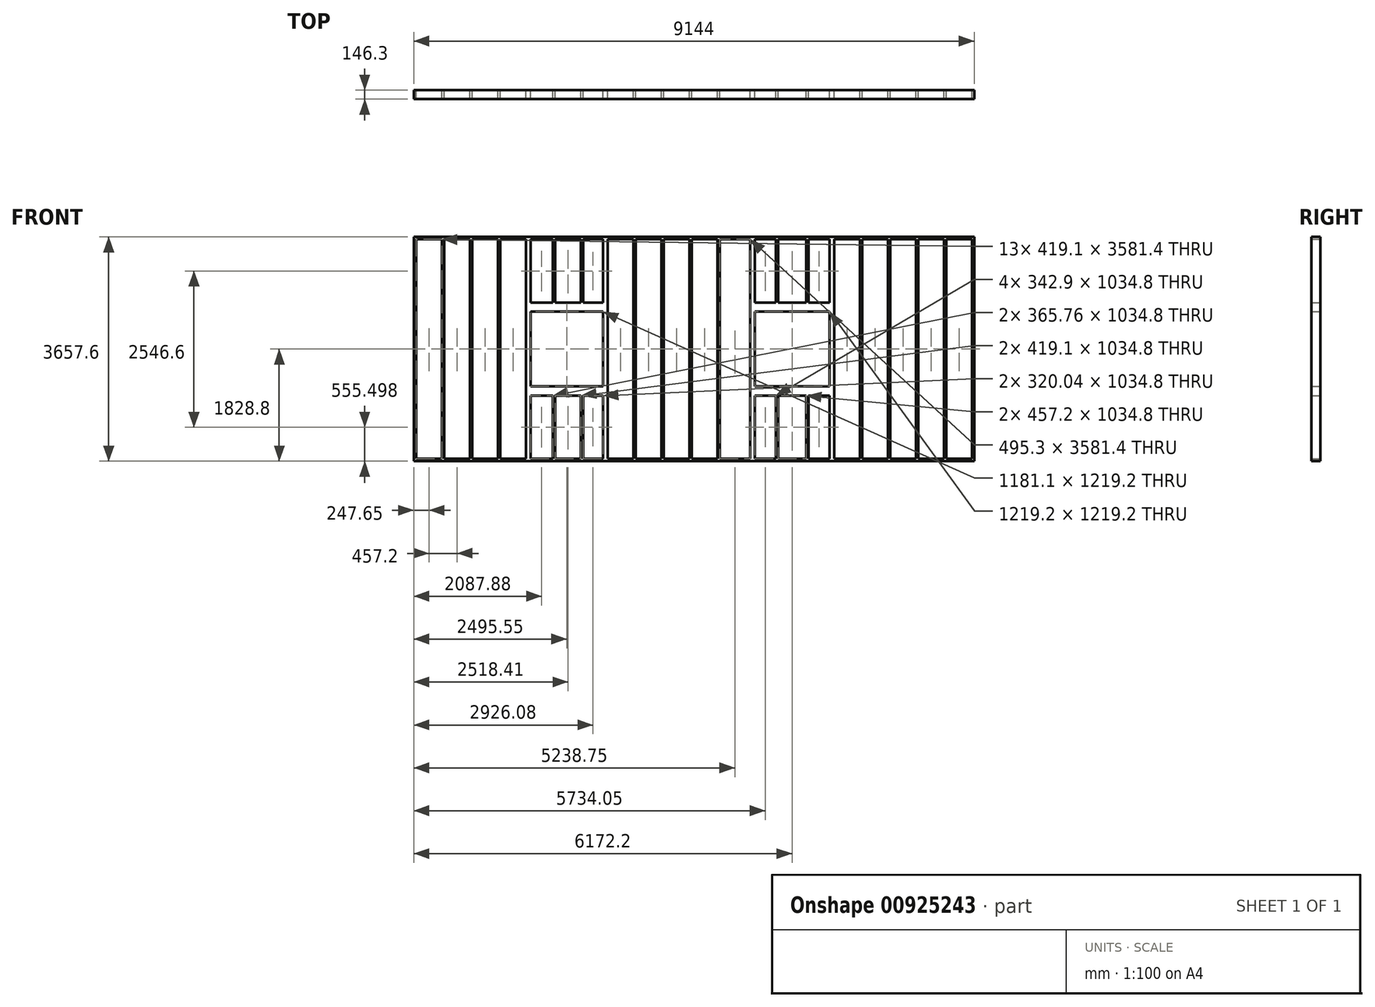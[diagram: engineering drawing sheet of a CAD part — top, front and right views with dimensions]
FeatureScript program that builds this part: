
annotation { "Feature Type Name" : "Feature", "Feature Type Description" : "" }
export const myFeature = defineFeature(function(context is Context, id is Id, definition is map)
    precondition{}
    {
        {
            var Q0;
            Q0=qCreatedBy(makeId("Front.planeOp"),FACE);
            var sketch = newSketch(context, id + "F0", { "sketchPlane" : qUnion([Q0])});
            skLineSegment(sketch, "E0.bottom", {"start": v(0, 0) * mm, "end": v(9144, 0) * mm});
            skLineSegment(sketch, "E0.top", {"start": v(0, 3657.6) * mm, "end": v(9144, 3657.6) * mm});
            skLineSegment(sketch, "E0.right", {"start": v(9144, 0) * mm, "end": v(9144, 3657.6) * mm});
            skLineSegment(sketch, "E1.2", {"start": v(9105.9, 38.1) * mm, "end": v(9105.9, 3619.5) * mm});
            skLineSegment(sketch, "E2.8.0.0", {"start": v(457.2, 3619.5) * mm, "end": v(457.2, 38.1) * mm});
            skLineSegment(sketch, "E2.8.0.1", {"start": v(495.3, 3619.5) * mm, "end": v(495.3, 38.1) * mm});
            skLineSegment(sketch, "E2.9.0.0", {"start": v(914.4, 3619.5) * mm, "end": v(914.4, 38.1) * mm});
            skLineSegment(sketch, "E2.9.0.1", {"start": v(952.5, 3619.5) * mm, "end": v(952.5, 38.1) * mm});
            skLineSegment(sketch, "E2.10.0.0", {"start": v(1371.6, 3619.5) * mm, "end": v(1371.6, 38.1) * mm});
            skLineSegment(sketch, "E2.10.0.1", {"start": v(1409.7, 3619.5) * mm, "end": v(1409.7, 38.1) * mm});
            skLineSegment(sketch, "E2.11.0.0", {"start": v(1828.8, 3619.5) * mm, "end": v(1828.8, 38.1) * mm});
            skLineSegment(sketch, "E2.11.0.1", {"start": v(1905, 3619.5) * mm, "end": v(1905, 2584.7) * mm});
            skLineSegment(sketch, "E2.12.0.0", {"start": v(2270.76, 3619.5) * mm, "end": v(2270.76, 2584.7) * mm});
            skLineSegment(sketch, "E2.12.0.1", {"start": v(2308.86, 3619.5) * mm, "end": v(2308.86, 2584.7) * mm});
            skLineSegment(sketch, "E2.13.0.0", {"start": v(2727.96, 3619.5) * mm, "end": v(2727.96, 2584.7) * mm});
            skLineSegment(sketch, "E2.13.0.1", {"start": v(2766.06, 3619.5) * mm, "end": v(2766.06, 2584.7) * mm});
            skLineSegment(sketch, "E2.14.0.0", {"start": v(3086.1, 3619.5) * mm, "end": v(3086.1, 2584.7) * mm});
            skLineSegment(sketch, "E2.14.0.1", {"start": v(3162.3, 3619.5) * mm, "end": v(3162.3, 38.1) * mm});
            skLineSegment(sketch, "E2.15.0.0", {"start": v(3581.4, 3619.5) * mm, "end": v(3581.4, 38.1) * mm});
            skLineSegment(sketch, "E2.15.0.1", {"start": v(3619.5, 3619.5) * mm, "end": v(3619.5, 38.1) * mm});
            skLineSegment(sketch, "E2.16.0.0", {"start": v(4038.6, 3619.5) * mm, "end": v(4038.6, 38.1) * mm});
            skLineSegment(sketch, "E2.16.0.1", {"start": v(4076.7, 3619.5) * mm, "end": v(4076.7, 38.1) * mm});
            skLineSegment(sketch, "E2.17.0.0", {"start": v(4495.8, 3619.5) * mm, "end": v(4495.8, 38.1) * mm});
            skLineSegment(sketch, "E2.17.0.1", {"start": v(4533.9, 3619.5) * mm, "end": v(4533.9, 38.1) * mm});
            skLineSegment(sketch, "E2.18.0.0", {"start": v(5486.4, 3619.5) * mm, "end": v(5486.4, 38.1) * mm});
            skLineSegment(sketch, "E2.18.0.1", {"start": v(5562.6, 3619.5) * mm, "end": v(5562.6, 2584.7) * mm});
            skLineSegment(sketch, "E2.19.0.0", {"start": v(5905.5, 3619.5) * mm, "end": v(5905.5, 2584.7) * mm});
            skLineSegment(sketch, "E2.19.0.1", {"start": v(5943.6, 3619.5) * mm, "end": v(5943.6, 2584.7) * mm});
            skLineSegment(sketch, "E2.20.0.0", {"start": v(6400.8, 3619.5) * mm, "end": v(6400.8, 2584.7) * mm});
            skLineSegment(sketch, "E2.20.0.1", {"start": v(6438.9, 3619.5) * mm, "end": v(6438.9, 2584.7) * mm});
            skLineSegment(sketch, "E2.21.0.0", {"start": v(6781.8, 3619.5) * mm, "end": v(6781.8, 2584.7) * mm});
            skLineSegment(sketch, "E2.21.0.1", {"start": v(6858, 3619.5) * mm, "end": v(6858, 38.1) * mm});
            skLineSegment(sketch, "E2.22.0.0", {"start": v(7277.1, 3619.5) * mm, "end": v(7277.1, 38.1) * mm});
            skLineSegment(sketch, "E2.22.0.1", {"start": v(7315.2, 3619.5) * mm, "end": v(7315.2, 38.1) * mm});
            skLineSegment(sketch, "E2.23.0.0", {"start": v(7734.3, 3619.5) * mm, "end": v(7734.3, 38.1) * mm});
            skLineSegment(sketch, "E2.23.0.1", {"start": v(7772.4, 3619.5) * mm, "end": v(7772.4, 38.1) * mm});
            skLineSegment(sketch, "E2.24.0.0", {"start": v(8191.5, 3619.5) * mm, "end": v(8191.5, 38.1) * mm});
            skLineSegment(sketch, "E2.24.0.1", {"start": v(8229.6, 3619.5) * mm, "end": v(8229.6, 38.1) * mm});
            skLineSegment(sketch, "E2.25.0.0", {"start": v(8648.7, 3619.5) * mm, "end": v(8648.7, 38.1) * mm});
            skLineSegment(sketch, "E2.25.0.1", {"start": v(8686.8, 3619.5) * mm, "end": v(8686.8, 38.1) * mm});
            skLineSegment(sketch, "E3.trimOffspring", {"start": v(38.1, 3619.5) * mm, "end": v(457.2, 3619.5) * mm});
            skLineSegment(sketch, "E4.trimOffspring", {"start": v(495.3, 3619.5) * mm, "end": v(914.4, 3619.5) * mm});
            skLineSegment(sketch, "E5.trimOffspring", {"start": v(952.5, 3619.5) * mm, "end": v(1371.6, 3619.5) * mm});
            skLineSegment(sketch, "E6.trimOffspring", {"start": v(1409.7, 3619.5) * mm, "end": v(1828.8, 3619.5) * mm});
            skLineSegment(sketch, "E7.trimOffspring", {"start": v(1905, 3619.5) * mm, "end": v(2270.76, 3619.5) * mm});
            skLineSegment(sketch, "E8.trimOffspring", {"start": v(2308.86, 3619.5) * mm, "end": v(2727.96, 3619.5) * mm});
            skLineSegment(sketch, "E9.trimOffspring", {"start": v(2766.06, 3619.5) * mm, "end": v(3086.1, 3619.5) * mm});
            skLineSegment(sketch, "E10.trimOffspring", {"start": v(3162.3, 3619.5) * mm, "end": v(3581.4, 3619.5) * mm});
            skLineSegment(sketch, "E11.trimOffspring", {"start": v(3619.5, 3619.5) * mm, "end": v(4038.6, 3619.5) * mm});
            skLineSegment(sketch, "E12.trimOffspring", {"start": v(4076.7, 3619.5) * mm, "end": v(4495.8, 3619.5) * mm});
            skLineSegment(sketch, "E13.trimOffspring", {"start": v(4533.9, 3619.5) * mm, "end": v(5486.4, 3619.5) * mm});
            skLineSegment(sketch, "E14.trimOffspring", {"start": v(5562.6, 3619.5) * mm, "end": v(5905.5, 3619.5) * mm});
            skLineSegment(sketch, "E15.trimOffspring", {"start": v(5943.6, 3619.5) * mm, "end": v(6400.8, 3619.5) * mm});
            skLineSegment(sketch, "E16.trimOffspring", {"start": v(6438.9, 3619.5) * mm, "end": v(6781.8, 3619.5) * mm});
            skLineSegment(sketch, "E17.trimOffspring", {"start": v(6858, 3619.5) * mm, "end": v(7277.1, 3619.5) * mm});
            skLineSegment(sketch, "E18.trimOffspring", {"start": v(7315.2, 3619.5) * mm, "end": v(7734.3, 3619.5) * mm});
            skLineSegment(sketch, "E19.trimOffspring", {"start": v(7772.4, 3619.5) * mm, "end": v(8191.5, 3619.5) * mm});
            skLineSegment(sketch, "E20.trimOffspring", {"start": v(8229.6, 3619.5) * mm, "end": v(8648.7, 3619.5) * mm});
            skLineSegment(sketch, "E21.trimOffspring", {"start": v(8686.8, 3619.5) * mm, "end": v(9105.9, 3619.5) * mm});
            skLineSegment(sketch, "E22.trimOffspring", {"start": v(8686.8, 38.1) * mm, "end": v(9105.9, 38.1) * mm});
            skLineSegment(sketch, "E23.trimOffspring", {"start": v(8229.6, 38.1) * mm, "end": v(8648.7, 38.1) * mm});
            skLineSegment(sketch, "E24.trimOffspring", {"start": v(7772.4, 38.1) * mm, "end": v(8191.5, 38.1) * mm});
            skLineSegment(sketch, "E25.trimOffspring", {"start": v(7315.2, 38.1) * mm, "end": v(7734.3, 38.1) * mm});
            skLineSegment(sketch, "E26.trimOffspring", {"start": v(6858, 38.1) * mm, "end": v(7277.1, 38.1) * mm});
            skLineSegment(sketch, "E27.trimOffspring", {"start": v(6438.9, 38.1) * mm, "end": v(6781.8, 38.1) * mm});
            skLineSegment(sketch, "E28.trimOffspring", {"start": v(5943.6, 38.1) * mm, "end": v(6400.8, 38.1) * mm});
            skLineSegment(sketch, "E29.trimOffspring", {"start": v(5562.6, 38.1) * mm, "end": v(5905.5, 38.1) * mm});
            skLineSegment(sketch, "E30.trimOffspring", {"start": v(4533.9, 38.1) * mm, "end": v(4953, 38.1) * mm});
            skLineSegment(sketch, "E31.trimOffspring", {"start": v(4076.7, 38.1) * mm, "end": v(4495.8, 38.1) * mm});
            skLineSegment(sketch, "E32.trimOffspring", {"start": v(3619.5, 38.1) * mm, "end": v(4038.6, 38.1) * mm});
            skLineSegment(sketch, "E33.trimOffspring", {"start": v(3162.3, 38.1) * mm, "end": v(3581.4, 38.1) * mm});
            skLineSegment(sketch, "E34.trimOffspring", {"start": v(2766.06, 38.1) * mm, "end": v(3086.1, 38.1) * mm});
            skLineSegment(sketch, "E35.trimOffspring", {"start": v(2308.86, 38.1) * mm, "end": v(2727.96, 38.1) * mm});
            skLineSegment(sketch, "E36.trimOffspring", {"start": v(1905, 38.1) * mm, "end": v(2270.76, 38.1) * mm});
            skLineSegment(sketch, "E37.trimOffspring", {"start": v(1409.7, 38.1) * mm, "end": v(1828.8, 38.1) * mm});
            skLineSegment(sketch, "E38.trimOffspring", {"start": v(952.5, 38.1) * mm, "end": v(1371.6, 38.1) * mm});
            skLineSegment(sketch, "E39.trimOffspring", {"start": v(495.3, 38.1) * mm, "end": v(914.4, 38.1) * mm});
            skLineSegment(sketch, "E40.trimOffspring", {"start": v(38.1, 38.1) * mm, "end": v(457.2, 38.1) * mm});
            skLineSegment(sketch, "E41.bottom", {"start": v(1905, 2438.4) * mm, "end": v(2270.76, 2438.4) * mm});
            skLineSegment(sketch, "E41.top", {"start": v(1905, 1219.2) * mm, "end": v(2766.06, 1219.2) * mm});
            skLineSegment(sketch, "E41.left", {"start": v(1905, 2438.4) * mm, "end": v(1905, 1219.2) * mm});
            skLineSegment(sketch, "E41.right", {"start": v(3086.1, 2438.4) * mm, "end": v(3086.1, 1219.2) * mm});
            skLineSegment(sketch, "E42.trimOffspring", {"start": v(1905, 1072.9) * mm, "end": v(1905, 38.1) * mm});
            skLineSegment(sketch, "E43.trimOffspring", {"start": v(3086.1, 1072.9) * mm, "end": v(3086.1, 38.1) * mm});
            skLineSegment(sketch, "E44", {"start": v(1905, 1072.9) * mm, "end": v(2270.76, 1072.9) * mm});
            skLineSegment(sketch, "E45", {"start": v(1905, 2584.7) * mm, "end": v(2270.76, 2584.7) * mm});
            skLineSegment(sketch, "E46.trimOffspring", {"start": v(2270.76, 1072.9) * mm, "end": v(2270.76, 38.1) * mm});
            skLineSegment(sketch, "E47.trimOffspring", {"start": v(2308.86, 1072.9) * mm, "end": v(2308.86, 38.1) * mm});
            skLineSegment(sketch, "E48.trimOffspring", {"start": v(2727.96, 1072.9) * mm, "end": v(2727.96, 38.1) * mm});
            skLineSegment(sketch, "E49.trimOffspring", {"start": v(2766.06, 1072.9) * mm, "end": v(2766.06, 38.1) * mm});
            skLineSegment(sketch, "E50.trimOffspring", {"start": v(2308.86, 1219.2) * mm, "end": v(2727.96, 1219.2) * mm});
            skLineSegment(sketch, "E51.trimOffspring", {"start": v(2308.86, 1072.9) * mm, "end": v(2727.96, 1072.9) * mm});
            skLineSegment(sketch, "E52.trimOffspring", {"start": v(2766.06, 1219.2) * mm, "end": v(3086.1, 1219.2) * mm});
            skLineSegment(sketch, "E53.trimOffspring", {"start": v(2766.06, 1072.9) * mm, "end": v(3086.1, 1072.9) * mm});
            skLineSegment(sketch, "E54.trimOffspring", {"start": v(2308.86, 2584.7) * mm, "end": v(2727.96, 2584.7) * mm});
            skLineSegment(sketch, "E55.trimOffspring", {"start": v(2766.06, 2584.7) * mm, "end": v(3086.1, 2584.7) * mm});
            skLineSegment(sketch, "E56.trimOffspring", {"start": v(2270.76, 2438.4) * mm, "end": v(2766.06, 2438.4) * mm});
            skLineSegment(sketch, "E57.trimOffspring", {"start": v(2766.06, 2438.4) * mm, "end": v(3086.1, 2438.4) * mm});
            skLineSegment(sketch, "E58", {"start": v(5852.16, 2438.4) * mm, "end": v(5890.26, 2438.4) * mm});
            skLineSegment(sketch, "E59", {"start": v(2270.76, 2438.4) * mm, "end": v(2727.96, 2438.4) * mm});
            skLineSegment(sketch, "E60.bottom", {"start": v(5562.6, 2438.4) * mm, "end": v(6781.8, 2438.4) * mm});
            skLineSegment(sketch, "E60.top", {"start": v(5562.6, 1219.2) * mm, "end": v(6781.8, 1219.2) * mm});
            skLineSegment(sketch, "E60.left", {"start": v(5562.6, 2438.4) * mm, "end": v(5562.6, 1219.2) * mm});
            skLineSegment(sketch, "E60.right", {"start": v(6781.8, 2438.4) * mm, "end": v(6781.8, 1219.2) * mm});
            skLineSegment(sketch, "E61.trimOffspring", {"start": v(5562.6, 1072.9) * mm, "end": v(5562.6, 38.1) * mm});
            skLineSegment(sketch, "E62.trimOffspring", {"start": v(6781.8, 1072.9) * mm, "end": v(6781.8, 38.1) * mm});
            skLineSegment(sketch, "E63", {"start": v(5562.6, 1072.9) * mm, "end": v(5905.5, 1072.9) * mm});
            skLineSegment(sketch, "E64", {"start": v(5562.6, 2584.7) * mm, "end": v(5905.5, 2584.7) * mm});
            skLineSegment(sketch, "E65.trimOffspring", {"start": v(5905.5, 1072.9) * mm, "end": v(5905.5, 38.1) * mm});
            skLineSegment(sketch, "E66.trimOffspring", {"start": v(5943.6, 1072.9) * mm, "end": v(5943.6, 38.1) * mm});
            skLineSegment(sketch, "E67.trimOffspring", {"start": v(6400.8, 1072.9) * mm, "end": v(6400.8, 38.1) * mm});
            skLineSegment(sketch, "E68.trimOffspring", {"start": v(6438.9, 1072.9) * mm, "end": v(6438.9, 38.1) * mm});
            skLineSegment(sketch, "E69.trimOffspring", {"start": v(5943.6, 1072.9) * mm, "end": v(6400.8, 1072.9) * mm});
            skLineSegment(sketch, "E70.trimOffspring", {"start": v(6438.9, 1072.9) * mm, "end": v(6781.8, 1072.9) * mm});
            skLineSegment(sketch, "E71.trimOffspring", {"start": v(5943.6, 2584.7) * mm, "end": v(6400.8, 2584.7) * mm});
            skLineSegment(sketch, "E72.trimOffspring", {"start": v(6438.9, 2584.7) * mm, "end": v(6781.8, 2584.7) * mm});
            skLineSegment(sketch, "E73", {"start": v(0, 3657.6) * mm, "end": v(0, 0) * mm});
            skLineSegment(sketch, "E74", {"start": v(38.1, 38.1) * mm, "end": v(38.1, 3619.5) * mm});
            skLineSegment(sketch, "E75", {"start": v(4953, 3619.5) * mm, "end": v(4953, 38.1) * mm});
            skLineSegment(sketch, "E76", {"start": v(4991.1, 3619.5) * mm, "end": v(4991.1, 38.1) * mm});
            skLineSegment(sketch, "E77.trimOffspring", {"start": v(4991.1, 38.1) * mm, "end": v(5486.4, 38.1) * mm});
            skSolve(sketch);
        }
        {
            var Q0;
            Q0=qSketchRegion(id+"F0",true);
            extrude(context, id + "F1", {"entities" : qUnion([Q0]), "depth" : 146.3 * mm, "offsetDistance" : 30.48 * mm});
        }
    });
